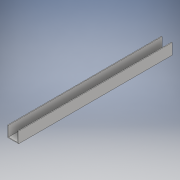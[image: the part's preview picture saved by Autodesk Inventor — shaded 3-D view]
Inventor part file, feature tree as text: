
AUTODESK INVENTOR PART (.ipt)
format: ipt  version: 2017 (Build 210142000, 142)  size: 100,352 bytes
history: native  units: in
note: dims shown in document units (in); Inventor stores cm internally (conversion verified against a paired STEP export)
features: sketch x2, extrude x1
ambient origin geometry x8: Origin, YZ Plane, XZ Plane, XY Plane, X Axis, Y Axis, Z Axis, Center Point
bodies: Solid1 (feature_tree)
feature tree (3):
  sketch  "Sketch1"  dims[d2=0.079in d3=1.26in]
  sketch  "Sketch2"  dims[d5=17.75in d6=0.0in]
  extrude  "Extrusion1"  Depth=1.26in
